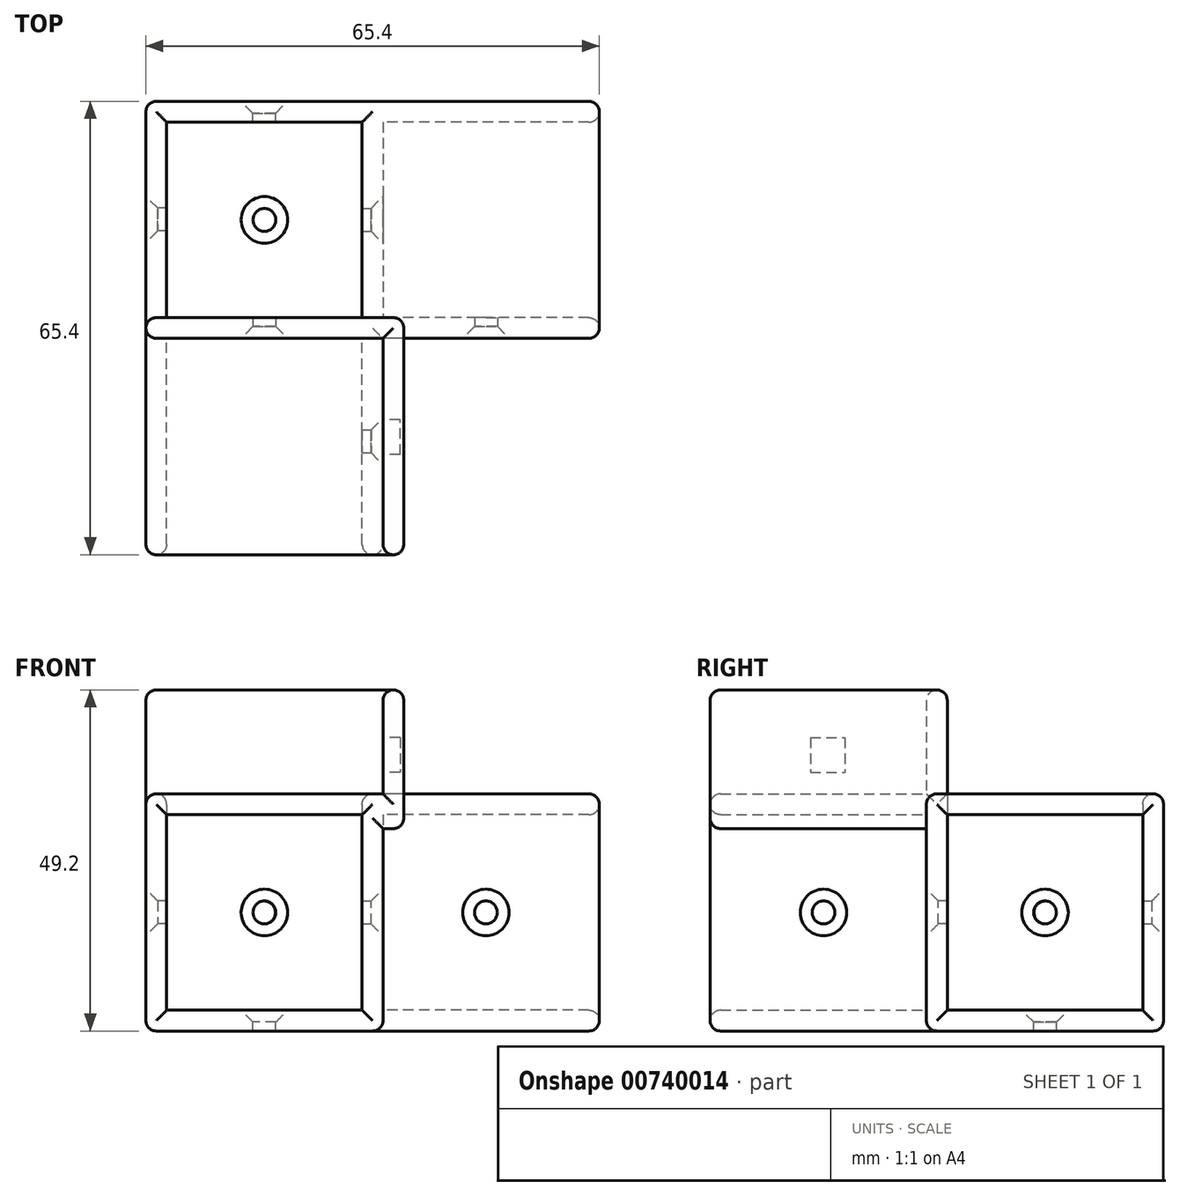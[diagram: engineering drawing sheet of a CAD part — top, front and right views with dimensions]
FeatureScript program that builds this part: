
annotation { "Feature Type Name" : "Feature", "Feature Type Description" : "" }
export const myFeature = defineFeature(function(context is Context, id is Id, definition is map)
    precondition{}
    {
        {
            var Q0;
            Q0=qCreatedBy(makeId("Top.planeOp"),FACE);
            var sketch = newSketch(context, id + "F0", { "sketchPlane" : qUnion([Q0])});
            skLineSegment(sketch, "E0.bottom", {"start": v(0, 0) * mm, "end": v(-28.2, 0) * mm});
            skLineSegment(sketch, "E0.top", {"start": v(0, 28.2) * mm, "end": v(-28.2, 28.2) * mm});
            skLineSegment(sketch, "E0.left", {"start": v(0, 0) * mm, "end": v(0, 28.2) * mm});
            skLineSegment(sketch, "E0.right", {"start": v(-28.2, 0) * mm, "end": v(-28.2, 28.2) * mm});
            skLineSegment(sketch, "E1.0", {"start": v(3, 31.2) * mm, "end": v(-31.2, 31.2) * mm});
            skLineSegment(sketch, "E1.1", {"start": v(3, -3) * mm, "end": v(3, 31.2) * mm});
            skLineSegment(sketch, "E1.2", {"start": v(3, -3) * mm, "end": v(-31.2, -3) * mm});
            skLineSegment(sketch, "E1.3", {"start": v(-31.2, -3) * mm, "end": v(-31.2, 31.2) * mm});
            skPoint(sketch, "E2", {"position": v(-14.1, 14.1) * mm});
            skSolve(sketch);
        }
        {
            var Q0;
            Q0=makeQuery(id+"F0.imprint","IMPRINT",FACE,{"disambiguationData":[TD([[makeQuery(id+"F0.imprint","IMPRINT",EDGE,{"derivedFrom":sQuery(id+"F0.wireOp",EDGE,"E0.bottom")}),1.0]])]});
            var Q1;
            Q1=makeQuery(id+"F0.imprint","IMPRINT",FACE,{"disambiguationData":[TD([[makeQuery(id+"F0.imprint","IMPRINT",EDGE,{"derivedFrom":sQuery(id+"F0.wireOp",EDGE,"E0.bottom")}),-1.0]])]});
            extrude(context, id + "F1", {"entities" : qUnion([Q0, Q1]), "oppositeDirection" : true, "depth" : 3 * mm, "offsetDistance" : 25 * mm});
        }
        {
            var Q0;
            Q0=makeQuery(id+"F0.imprint","IMPRINT",FACE,{"disambiguationData":[TD([[makeQuery(id+"F0.imprint","IMPRINT",EDGE,{"derivedFrom":sQuery(id+"F0.wireOp",EDGE,"E0.bottom")}),1.0]])]});
            extrude(context, id + "F2", {"entities" : qUnion([Q0]), "operationType" : NewBodyOperationType.ADD, "depth" : 31.2 * mm, "offsetDistance" : 25 * mm});
        }
        {
            var Q0;
            {var subQ0=sQuery(id+"F0.wireOp",EDGE,"E1.2");Q0=makeQuery(id+"F2.boolean.opBoolean","MERGE",FACE,{"derivedFrom":[makeQuery(id+"F1.opExtrude","SWEPT_FACE",FACE,{"disambiguationData":[OSD([subQ0])]}),makeQuery(id+"F2.opExtrude","SWEPT_FACE",FACE,{"disambiguationData":[OSD([subQ0])]})]});}
            var sketch = newSketch(context, id + "F3", { "sketchPlane" : qUnion([Q0])});
            skLineSegment(sketch, "E3.bottom", {"start": v(-31.2, 31.2) * mm, "end": v(3, 31.2) * mm});
            skLineSegment(sketch, "E3.top", {"start": v(-31.2, -3) * mm, "end": v(3, -3) * mm});
            skLineSegment(sketch, "E3.left", {"start": v(-31.2, 31.2) * mm, "end": v(-31.2, -3) * mm});
            skLineSegment(sketch, "E3.right", {"start": v(3, 31.2) * mm, "end": v(3, -3) * mm});
            skLineSegment(sketch, "E4.0", {"start": v(-28.2, 28.2) * mm, "end": v(0, 28.2) * mm});
            skLineSegment(sketch, "E4.1", {"start": v(-28.2, 28.2) * mm, "end": v(-28.2, 0) * mm});
            skLineSegment(sketch, "E4.2", {"start": v(-28.2, 0) * mm, "end": v(0, 0) * mm});
            skLineSegment(sketch, "E4.3", {"start": v(0, 28.2) * mm, "end": v(0, 0) * mm});
            skPoint(sketch, "E5", {"position": v(-14.1, 14.1) * mm});
            skSolve(sketch);
        }
        {
            var Q0;
            Q0=makeQuery(id+"F3.imprint","IMPRINT",FACE,{"disambiguationData":[TD([[makeQuery(id+"F3.imprint","IMPRINT",EDGE,{"derivedFrom":sQuery(id+"F3.wireOp",EDGE,"E3.bottom")}),1.0]])]});
            extrude(context, id + "F4", {"entities" : qUnion([Q0]), "operationType" : NewBodyOperationType.ADD, "depth" : 31.2 * mm, "offsetDistance" : 25 * mm});
        }
        {
            var Q0;
            {var subQ0=sQuery(id+"F0.wireOp",EDGE,"E1.1");Q0=makeQuery(id+"F4.boolean.opBoolean","MERGE",FACE,{"derivedFrom":[makeQuery(id+"F2.boolean.opBoolean","MERGE",FACE,{"derivedFrom":[makeQuery(id+"F1.opExtrude","SWEPT_FACE",FACE,{"disambiguationData":[OSD([subQ0])]}),makeQuery(id+"F2.opExtrude","SWEPT_FACE",FACE,{"disambiguationData":[OSD([subQ0])]})]}),makeQuery(id+"F4.opExtrude","SWEPT_FACE",FACE,{"disambiguationData":[OSD([sQuery(id+"F3.wireOp",EDGE,"E3.right")])]})]});}
            var sketch = newSketch(context, id + "F5", { "sketchPlane" : qUnion([Q0])});
            skLineSegment(sketch, "E6.bottom", {"start": v(31.2, 31.2) * mm, "end": v(-3, 31.2) * mm});
            skLineSegment(sketch, "E6.top", {"start": v(31.2, -3) * mm, "end": v(-3, -3) * mm});
            skLineSegment(sketch, "E6.left", {"start": v(31.2, 31.2) * mm, "end": v(31.2, -3) * mm});
            skLineSegment(sketch, "E6.right", {"start": v(-3, 31.2) * mm, "end": v(-3, -3) * mm});
            skLineSegment(sketch, "E7.0", {"start": v(28.2, 28.2) * mm, "end": v(0, 28.2) * mm});
            skLineSegment(sketch, "E7.1", {"start": v(28.2, 28.2) * mm, "end": v(28.2, 0) * mm});
            skLineSegment(sketch, "E7.2", {"start": v(28.2, 0) * mm, "end": v(0, 0) * mm});
            skLineSegment(sketch, "E7.3", {"start": v(0, 28.2) * mm, "end": v(0, 0) * mm});
            skPoint(sketch, "E8", {"position": v(14.1, 14.1) * mm});
            skSolve(sketch);
        }
        {
            var Q0;
            Q0=qSketchRegion(id+"F5",true);
            extrude(context, id + "F6", {"entities" : qUnion([Q0]), "operationType" : NewBodyOperationType.ADD, "depth" : 31.2 * mm, "offsetDistance" : 25 * mm});
        }
        {
            var Q0;
            Q0=sQuery(id+"F0.wireOp",VERTEX,"E2");
            var Q1;
            Q1=sQuery(id+"F5.wireOp",VERTEX,"E8");
            var Q2;
            Q2=sQuery(id+"F3.wireOp",VERTEX,"E5");
            var Q3;
            Q3=makeQuery(id+"F1.opExtrude","SWEPT_BODY",BODY,{"disambiguationData":[OSD([sQuery(id+"F0.wireOp",EDGE,"E1.0"),sQuery(id+"F0.wireOp",EDGE,"E1.1"),sQuery(id+"F0.wireOp",EDGE,"E1.2"),sQuery(id+"F0.wireOp",EDGE,"E1.3")])]});
            hole(context, id + "F7", {"style" : HoleStyle.C_SINK, "endStyle" : HoleEndStyle.BLIND, "standardTappedOrClearance" : lookupTablePath({ "standard" : "ISO", "fit" : "Normal", "size" : "M3", "type" : "Clearance" }), "standardBlindInLast" : lookupTablePath({ "fit" : "Standard", "standard" : "ISO", "size" : "M3", "type" : "Clearance" }), "holeDiameter" : 3.3 * mm, "cSinkDiameter" : 6.72 * mm, "cSinkAngle" : 90 * degree, "majorDiameter" : 5 * mm, "holeDepth" : 13.5 * mm, "isTappedThrough" : true, "tappedDepth" : 12 * mm, "tapClearance" : 3, "startFromSketch" : true, "locations" : qUnion([Q0, Q1, Q2]), "scope" : qUnion([Q3])});
        }
        {
            var Q0;
            {var subQ0=sQuery(id+"F3.wireOp",EDGE,"E3.bottom");var subQ3=sQuery(id+"F0.wireOp",EDGE,"E1.1");var subQ5=sQuery(id+"F3.wireOp",EDGE,"E3.right");Q0=makeQuery(id+"F6.boolean.opBoolean","SPLIT",FACE,{"disambiguationData":[TD([makeQuery(id+"F4.opExtrude","SWEPT_FACE",FACE,{"disambiguationData":[OSD([subQ0])]})])],"derivedFrom":makeQuery(id+"F4.boolean.opBoolean","MERGE",FACE,{"derivedFrom":[makeQuery(id+"F2.boolean.opBoolean","MERGE",FACE,{"derivedFrom":[makeQuery(id+"F1.opExtrude","SWEPT_FACE",FACE,{"disambiguationData":[OSD([subQ3])]}),makeQuery(id+"F2.opExtrude","SWEPT_FACE",FACE,{"disambiguationData":[OSD([subQ3])]})]}),makeQuery(id+"F4.opExtrude","SWEPT_FACE",FACE,{"disambiguationData":[OSD([subQ5])]})]})});}
            var sketch = newSketch(context, id + "F8", { "sketchPlane" : qUnion([Q0])});
            skPoint(sketch, "E9", {"position": v(-17.85, 14.1) * mm});
            skSolve(sketch);
        }
        {
            var Q0;
            Q0=makeQuery(id+"F6.opExtrude","SWEPT_FACE",FACE,{"disambiguationData":[OSD([sQuery(id+"F5.wireOp",EDGE,"E6.right")])]});
            var sketch = newSketch(context, id + "F9", { "sketchPlane" : qUnion([Q0])});
            skPoint(sketch, "E10", {"position": v(17.85, 14.1) * mm});
            skSolve(sketch);
        }
        {
            var Q0;
            Q0=sQuery(id+"F9.wireOp",VERTEX,"E10");
            var Q1;
            Q1=sQuery(id+"F8.wireOp",VERTEX,"E9");
            var Q2;
            Q2=makeQuery(id+"F1.opExtrude","SWEPT_BODY",BODY,{"disambiguationData":[OSD([sQuery(id+"F0.wireOp",EDGE,"E1.0"),sQuery(id+"F0.wireOp",EDGE,"E1.1"),sQuery(id+"F0.wireOp",EDGE,"E1.2"),sQuery(id+"F0.wireOp",EDGE,"E1.3")])]});
            hole(context, id + "F10", {"style" : HoleStyle.C_SINK, "endStyle" : HoleEndStyle.BLIND, "standardTappedOrClearance" : lookupTablePath({ "standard" : "ISO", "fit" : "Normal", "size" : "M3", "type" : "Clearance" }), "standardBlindInLast" : lookupTablePath({ "fit" : "Standard", "standard" : "ISO", "size" : "M3", "type" : "Clearance" }), "holeDiameter" : 3.3 * mm, "cSinkDiameter" : 6.72 * mm, "cSinkAngle" : 90 * degree, "majorDiameter" : 5 * mm, "holeDepth" : 13.5 * mm, "isTappedThrough" : true, "tappedDepth" : 12 * mm, "tapClearance" : 3, "startFromSketch" : true, "locations" : qUnion([Q0, Q1]), "scope" : qUnion([Q2])});
        }
        {
            var Q0;
            Q0=makeQuery(id+"F6.boolean.opBoolean","MERGE",FACE,{"derivedFrom":[makeQuery(id+"F4.boolean.opBoolean","MERGE",FACE,{"derivedFrom":[makeQuery(id+"F2.opExtrude","CAP_FACE",FACE,{"disambiguationData":[OSD([sQuery(id+"F0.wireOp",EDGE,"E0.bottom"),sQuery(id+"F0.wireOp",EDGE,"E0.top"),sQuery(id+"F0.wireOp",EDGE,"E0.left"),sQuery(id+"F0.wireOp",EDGE,"E0.right"),sQuery(id+"F0.wireOp",EDGE,"E1.0"),sQuery(id+"F0.wireOp",EDGE,"E1.1"),sQuery(id+"F0.wireOp",EDGE,"E1.2"),sQuery(id+"F0.wireOp",EDGE,"E1.3")])],"isStart":false}),makeQuery(id+"F4.opExtrude","SWEPT_FACE",FACE,{"disambiguationData":[OSD([sQuery(id+"F3.wireOp",EDGE,"E3.bottom")])]})]}),makeQuery(id+"F6.opExtrude","SWEPT_FACE",FACE,{"disambiguationData":[OSD([sQuery(id+"F5.wireOp",EDGE,"E6.bottom")])]})]});
            var sketch = newSketch(context, id + "F11", { "sketchPlane" : qUnion([Q0])});
            skLineSegment(sketch, "E11.bottom", {"start": v(6, 0) * mm, "end": v(-31.2, 0) * mm});
            skLineSegment(sketch, "E11.top", {"start": v(6, -3) * mm, "end": v(-31.2, -3) * mm});
            skLineSegment(sketch, "E11.right", {"start": v(-31.2, 0) * mm, "end": v(-31.2, -3) * mm});
            skLineSegment(sketch, "E12", {"start": v(6, -3) * mm, "end": v(6, 0) * mm});
            skSolve(sketch);
        }
        {
            var Q0;
            {var subQ5=sQuery(id+"F11.wireOp",EDGE,"E11.right");Q0=makeQuery(id+"F11.imprint","IMPRINT",FACE,{"disambiguationData":[TD([[makeQuery(id+"F11.imprint","IMPRINT",EDGE,{"derivedFrom":subQ5}),-1.0]])]});}
            extrude(context, id + "F12", {"entities" : qUnion([Q0]), "operationType" : NewBodyOperationType.ADD, "depth" : 15 * mm, "offsetDistance" : 25 * mm});
        }
        {
            var Q0;
            {var subQ0=sQuery(id+"F0.wireOp",EDGE,"E1.3");Q0=makeQuery(id+"F4.boolean.opBoolean","MERGE",FACE,{"derivedFrom":[makeQuery(id+"F2.boolean.opBoolean","MERGE",FACE,{"derivedFrom":[makeQuery(id+"F1.opExtrude","SWEPT_FACE",FACE,{"disambiguationData":[OSD([subQ0])]}),makeQuery(id+"F2.opExtrude","SWEPT_FACE",FACE,{"disambiguationData":[OSD([subQ0])]})]}),makeQuery(id+"F4.opExtrude","SWEPT_FACE",FACE,{"disambiguationData":[OSD([sQuery(id+"F3.wireOp",EDGE,"E3.left")])]})]});}
            var sketch = newSketch(context, id + "F13", { "sketchPlane" : qUnion([Q0])});
            skPoint(sketch, "E13", {"position": v(-14.15, 14.1) * mm});
            skSolve(sketch);
        }
        {
            var Q0;
            {var subQ0=sQuery(id+"F0.wireOp",EDGE,"E1.0");Q0=makeQuery(id+"F6.boolean.opBoolean","MERGE",FACE,{"derivedFrom":[makeQuery(id+"F2.boolean.opBoolean","MERGE",FACE,{"derivedFrom":[makeQuery(id+"F1.opExtrude","SWEPT_FACE",FACE,{"disambiguationData":[OSD([subQ0])]}),makeQuery(id+"F2.opExtrude","SWEPT_FACE",FACE,{"disambiguationData":[OSD([subQ0])]})]}),makeQuery(id+"F6.opExtrude","SWEPT_FACE",FACE,{"disambiguationData":[OSD([sQuery(id+"F5.wireOp",EDGE,"E6.left")])]})]});}
            var sketch = newSketch(context, id + "F14", { "sketchPlane" : qUnion([Q0])});
            skPoint(sketch, "E14", {"position": v(14.15, 14.1) * mm});
            skPoint(sketch, "E14.positionSnap0", {"position": v(31.2, 14.1) * mm});
            skSolve(sketch);
        }
        {
            var Q0;
            Q0=sQuery(id+"F13.wireOp",VERTEX,"E13");
            var Q1;
            Q1=sQuery(id+"F14.wireOp",VERTEX,"E14");
            var Q2;
            Q2=makeQuery(id+"F1.opExtrude","SWEPT_BODY",BODY,{"disambiguationData":[OSD([sQuery(id+"F0.wireOp",EDGE,"E1.0"),sQuery(id+"F0.wireOp",EDGE,"E1.1"),sQuery(id+"F0.wireOp",EDGE,"E1.2"),sQuery(id+"F0.wireOp",EDGE,"E1.3")])]});
            hole(context, id + "F15", {"style" : HoleStyle.C_SINK, "endStyle" : HoleEndStyle.BLIND, "standardTappedOrClearance" : lookupTablePath({ "standard" : "ISO", "fit" : "Normal", "size" : "M3", "type" : "Clearance" }), "standardBlindInLast" : lookupTablePath({ "fit" : "Standard", "standard" : "ISO", "size" : "M3", "type" : "Clearance" }), "holeDiameter" : 3.3 * mm, "cSinkDiameter" : 6.72 * mm, "cSinkAngle" : 90 * degree, "majorDiameter" : 5 * mm, "holeDepth" : 13.5 * mm, "isTappedThrough" : true, "tappedDepth" : 12 * mm, "tapClearance" : 3, "startFromSketch" : true, "locations" : qUnion([Q0, Q1]), "scope" : qUnion([Q2])});
        }
        {
            var Q0;
            {var subQ0=sQuery(id+"F3.wireOp",EDGE,"E3.bottom");var subQ3=sQuery(id+"F0.wireOp",EDGE,"E1.1");var subQ5=sQuery(id+"F3.wireOp",EDGE,"E3.right");Q0=makeQuery(id+"F6.boolean.opBoolean","SPLIT",FACE,{"disambiguationData":[TD([makeQuery(id+"F4.opExtrude","SWEPT_FACE",FACE,{"disambiguationData":[OSD([subQ0])]})])],"derivedFrom":makeQuery(id+"F4.boolean.opBoolean","MERGE",FACE,{"derivedFrom":[makeQuery(id+"F2.boolean.opBoolean","MERGE",FACE,{"derivedFrom":[makeQuery(id+"F1.opExtrude","SWEPT_FACE",FACE,{"disambiguationData":[OSD([subQ3])]}),makeQuery(id+"F2.opExtrude","SWEPT_FACE",FACE,{"disambiguationData":[OSD([subQ3])]})]}),makeQuery(id+"F4.opExtrude","SWEPT_FACE",FACE,{"disambiguationData":[OSD([subQ5])]})]})});}
            var sketch = newSketch(context, id + "F16", { "sketchPlane" : qUnion([Q0])});
            skLineSegment(sketch, "E15.bottom", {"start": v(-34.2, 26.2) * mm, "end": v(-3, 26.2) * mm});
            skLineSegment(sketch, "E15.top", {"start": v(-34.2, 46.2) * mm, "end": v(-3, 46.2) * mm});
            skLineSegment(sketch, "E15.left", {"start": v(-34.2, 26.2) * mm, "end": v(-34.2, 46.2) * mm});
            skLineSegment(sketch, "E15.right", {"start": v(-3, 26.2) * mm, "end": v(-3, 46.2) * mm});
            skSolve(sketch);
        }
        {
            var Q0;
            {var subQ0=sQuery(id+"F16.wireOp",EDGE,"E15.bottom");Q0=makeQuery(id+"F16.imprint","IMPRINT",FACE,{"disambiguationData":[TD([[makeQuery(id+"F16.imprint","IMPRINT",EDGE,{"derivedFrom":subQ0}),1.0]])]});}
            var Q1;
            {var subQ0=sQuery(id+"F16.wireOp",EDGE,"E15.top");Q1=makeQuery(id+"F16.imprint","IMPRINT",FACE,{"disambiguationData":[TD([[makeQuery(id+"F16.imprint","IMPRINT",EDGE,{"derivedFrom":subQ0}),-1.0]])]});}
            extrude(context, id + "F17", {"entities" : qUnion([Q0, Q1]), "operationType" : NewBodyOperationType.ADD, "depth" : 3 * mm, "offsetDistance" : 25 * mm});
        }
        {
            var Q0;
            Q0=makeQuery(id+"F12.opExtrude","SWEPT_EDGE",EDGE,{"disambiguationData":[OSD([sQuery(id+"F0.wireOp",EDGE,"E1.3"),sQuery(id+"F3.wireOp",EDGE,"E3.bottom"),sQuery(id+"F3.wireOp",EDGE,"E3.left"),sQuery(id+"F11.wireOp",EDGE,"E11.bottom"),sQuery(id+"F11.wireOp",EDGE,"E11.right")])]});
            var Q1;
            Q1=makeQuery(id+"F12.opExtrude","SWEPT_EDGE",EDGE,{"disambiguationData":[OSD([sQuery(id+"F0.wireOp",EDGE,"E1.3"),sQuery(id+"F3.wireOp",EDGE,"E3.bottom"),sQuery(id+"F3.wireOp",EDGE,"E3.left"),sQuery(id+"F11.wireOp",EDGE,"E11.top"),sQuery(id+"F11.wireOp",EDGE,"E11.right")])]});
            var Q2;
            Q2=makeQuery(id+"F12.opExtrude","CAP_EDGE",EDGE,{"disambiguationData":[OSD([sQuery(id+"F11.wireOp",EDGE,"E11.right")])],"isStart":false});
            var Q3;
            Q3=makeQuery(id+"F17.opExtrude","SWEPT_EDGE",EDGE,{"disambiguationData":[OSD([sQuery(id+"F16.wireOp",EDGE,"E15.top"),sQuery(id+"F16.wireOp",EDGE,"E15.left")])]});
            var Q4;
            Q4=makeQuery(id+"F17.opExtrude","CAP_EDGE",EDGE,{"disambiguationData":[OSD([sQuery(id+"F16.wireOp",EDGE,"E15.left")])],"isStart":true});
            var Q5;
            Q5=makeQuery(id+"F17.opExtrude","CAP_EDGE",EDGE,{"disambiguationData":[OSD([sQuery(id+"F16.wireOp",EDGE,"E15.top")])],"isStart":true});
            var Q6;
            Q6=makeQuery(id+"F12.opExtrude","CAP_EDGE",EDGE,{"disambiguationData":[OSD([sQuery(id+"F11.wireOp",EDGE,"E11.top")])],"isStart":false});
            var Q7;
            Q7=makeQuery(id+"F12.opExtrude","CAP_EDGE",EDGE,{"disambiguationData":[OSD([sQuery(id+"F11.wireOp",EDGE,"E11.bottom")])],"isStart":false});
            var Q8;
            Q8=makeQuery(id+"F17.opExtrude","CAP_EDGE",EDGE,{"disambiguationData":[OSD([sQuery(id+"F16.wireOp",EDGE,"E15.left")])],"isStart":false});
            var Q9;
            Q9=makeQuery(id+"F17.boolean.opBoolean","MERGE",EDGE,{"derivedFrom":[makeQuery(id+"F12.opExtrude","CAP_EDGE",EDGE,{"disambiguationData":[OSD([sQuery(id+"F11.wireOp",EDGE,"E12")])],"isStart":false}),makeQuery(id+"F17.opExtrude","CAP_EDGE",EDGE,{"disambiguationData":[OSD([sQuery(id+"F16.wireOp",EDGE,"E15.top")])],"isStart":false})]});
            var Q10;
            Q10=makeQuery(id+"F4.opExtrude","CAP_EDGE",EDGE,{"disambiguationData":[OSD([sQuery(id+"F3.wireOp",EDGE,"E3.bottom")])],"isStart":false});
            var Q11;
            Q11=makeQuery(id+"F4.opExtrude","CAP_EDGE",EDGE,{"disambiguationData":[OSD([sQuery(id+"F3.wireOp",EDGE,"E3.left")])],"isStart":false});
            var Q12;
            Q12=makeQuery(id+"F4.opExtrude","CAP_EDGE",EDGE,{"disambiguationData":[OSD([sQuery(id+"F3.wireOp",EDGE,"E4.1")])],"isStart":false});
            var Q13;
            Q13=makeQuery(id+"F4.opExtrude","CAP_EDGE",EDGE,{"disambiguationData":[OSD([sQuery(id+"F3.wireOp",EDGE,"E3.top")])],"isStart":false});
            var Q14;
            Q14=makeQuery(id+"F4.opExtrude","CAP_EDGE",EDGE,{"disambiguationData":[OSD([sQuery(id+"F3.wireOp",EDGE,"E4.2")])],"isStart":true});
            var Q15;
            Q15=makeQuery(id+"F4.opExtrude","CAP_EDGE",EDGE,{"disambiguationData":[OSD([sQuery(id+"F3.wireOp",EDGE,"E3.right")])],"isStart":false});
            var Q16;
            Q16=makeQuery(id+"F4.opExtrude","CAP_EDGE",EDGE,{"disambiguationData":[OSD([sQuery(id+"F3.wireOp",EDGE,"E4.3")])],"isStart":false});
            var Q17;
            Q17=makeQuery(id+"F17.opExtrude","CAP_EDGE",EDGE,{"disambiguationData":[OSD([sQuery(id+"F16.wireOp",EDGE,"E15.bottom")])],"isStart":false});
            var Q18;
            Q18=makeQuery(id+"F17.opExtrude","CAP_EDGE",EDGE,{"disambiguationData":[OSD([sQuery(id+"F16.wireOp",EDGE,"E15.bottom")])],"isStart":true});
            var Q19;
            Q19=makeQuery(id+"F17.opExtrude","CAP_EDGE",EDGE,{"disambiguationData":[OSD([sQuery(id+"F16.wireOp",EDGE,"E15.right")])],"isStart":false});
            var Q20;
            Q20=makeQuery(id+"F6.opExtrude","CAP_EDGE",EDGE,{"disambiguationData":[OSD([sQuery(id+"F5.wireOp",EDGE,"E6.right")])],"isStart":true});
            var Q21;
            Q21=makeQuery(id+"F4.boolean.opBoolean","MERGE",EDGE,{"derivedFrom":[makeQuery(id+"F1.opExtrude","CAP_EDGE",EDGE,{"disambiguationData":[OSD([sQuery(id+"F0.wireOp",EDGE,"E1.1")])],"isStart":false}),makeQuery(id+"F4.opExtrude","SWEPT_EDGE",EDGE,{"disambiguationData":[OSD([sQuery(id+"F3.wireOp",EDGE,"E3.top"),sQuery(id+"F3.wireOp",EDGE,"E3.right")])]})]});
            var Q22;
            Q22=makeQuery(id+"F4.boolean.opBoolean","MERGE",EDGE,{"derivedFrom":[makeQuery(id+"F1.opExtrude","CAP_EDGE",EDGE,{"disambiguationData":[OSD([sQuery(id+"F0.wireOp",EDGE,"E1.3")])],"isStart":false}),makeQuery(id+"F4.opExtrude","SWEPT_EDGE",EDGE,{"disambiguationData":[OSD([sQuery(id+"F3.wireOp",EDGE,"E3.top"),sQuery(id+"F3.wireOp",EDGE,"E3.left")])]})]});
            var Q23;
            Q23=makeQuery(id+"F6.opExtrude","SWEPT_EDGE",EDGE,{"disambiguationData":[OSD([sQuery(id+"F0.wireOp",EDGE,"E1.1"),sQuery(id+"F3.wireOp",EDGE,"E3.bottom"),sQuery(id+"F3.wireOp",EDGE,"E3.right"),sQuery(id+"F5.wireOp",EDGE,"E6.bottom"),sQuery(id+"F5.wireOp",EDGE,"E6.right")])]});
            var Q24;
            Q24=makeQuery(id+"F6.opExtrude","CAP_EDGE",EDGE,{"disambiguationData":[OSD([sQuery(id+"F5.wireOp",EDGE,"E6.right")])],"isStart":false});
            var Q25;
            Q25=makeQuery(id+"F6.opExtrude","CAP_EDGE",EDGE,{"disambiguationData":[OSD([sQuery(id+"F5.wireOp",EDGE,"E7.3")])],"isStart":false});
            var Q26;
            Q26=makeQuery(id+"F6.opExtrude","CAP_EDGE",EDGE,{"disambiguationData":[OSD([sQuery(id+"F5.wireOp",EDGE,"E6.top")])],"isStart":false});
            var Q27;
            Q27=makeQuery(id+"F6.opExtrude","CAP_EDGE",EDGE,{"disambiguationData":[OSD([sQuery(id+"F5.wireOp",EDGE,"E7.2")])],"isStart":false});
            var Q28;
            Q28=makeQuery(id+"F6.opExtrude","CAP_EDGE",EDGE,{"disambiguationData":[OSD([sQuery(id+"F5.wireOp",EDGE,"E6.left")])],"isStart":false});
            var Q29;
            Q29=makeQuery(id+"F6.opExtrude","CAP_EDGE",EDGE,{"disambiguationData":[OSD([sQuery(id+"F5.wireOp",EDGE,"E7.1")])],"isStart":false});
            var Q30;
            Q30=makeQuery(id+"F6.opExtrude","CAP_EDGE",EDGE,{"disambiguationData":[OSD([sQuery(id+"F5.wireOp",EDGE,"E7.0")])],"isStart":false});
            var Q31;
            Q31=makeQuery(id+"F2.opExtrude","CAP_EDGE",EDGE,{"disambiguationData":[OSD([sQuery(id+"F0.wireOp",EDGE,"E0.left")])],"isStart":false});
            var Q32;
            Q32=makeQuery(id+"F2.opExtrude","CAP_EDGE",EDGE,{"disambiguationData":[OSD([sQuery(id+"F0.wireOp",EDGE,"E0.top")])],"isStart":false});
            var Q33;
            Q33=makeQuery(id+"F6.boolean.opBoolean","MERGE",EDGE,{"derivedFrom":[makeQuery(id+"F2.opExtrude","CAP_EDGE",EDGE,{"disambiguationData":[OSD([sQuery(id+"F0.wireOp",EDGE,"E1.0")])],"isStart":false}),makeQuery(id+"F6.opExtrude","SWEPT_EDGE",EDGE,{"disambiguationData":[OSD([sQuery(id+"F5.wireOp",EDGE,"E6.bottom"),sQuery(id+"F5.wireOp",EDGE,"E6.left")])]})]});
            var Q34;
            Q34=makeQuery(id+"F2.opExtrude","CAP_EDGE",EDGE,{"disambiguationData":[OSD([sQuery(id+"F0.wireOp",EDGE,"E0.right")])],"isStart":false});
            var Q35;
            {var subQ0=sQuery(id+"F0.wireOp",EDGE,"E1.3");var subQ1=sQuery(id+"F0.wireOp",EDGE,"E1.0");Q35=makeQuery(id+"F2.boolean.opBoolean","MERGE",EDGE,{"derivedFrom":[makeQuery(id+"F1.opExtrude","SWEPT_EDGE",EDGE,{"disambiguationData":[OSD([subQ1,subQ0])]}),makeQuery(id+"F2.opExtrude","SWEPT_EDGE",EDGE,{"disambiguationData":[OSD([subQ1,subQ0])]})]});}
            var Q36;
            Q36=makeQuery(id+"F6.boolean.opBoolean","MERGE",EDGE,{"derivedFrom":[makeQuery(id+"F1.opExtrude","CAP_EDGE",EDGE,{"disambiguationData":[OSD([sQuery(id+"F0.wireOp",EDGE,"E1.0")])],"isStart":false}),makeQuery(id+"F6.opExtrude","SWEPT_EDGE",EDGE,{"disambiguationData":[OSD([sQuery(id+"F5.wireOp",EDGE,"E6.top"),sQuery(id+"F5.wireOp",EDGE,"E6.left")])]})]});
            var Q37;
            Q37=makeQuery(id+"F6.opExtrude","SWEPT_EDGE",EDGE,{"disambiguationData":[OSD([sQuery(id+"F0.wireOp",EDGE,"E1.1"),sQuery(id+"F3.wireOp",EDGE,"E3.top"),sQuery(id+"F3.wireOp",EDGE,"E3.right"),sQuery(id+"F5.wireOp",EDGE,"E6.top"),sQuery(id+"F5.wireOp",EDGE,"E6.right")])]});
            var Q38;
            {var subQ0=sQuery(id+"F0.wireOp",EDGE,"E0.left");var subQ1=sQuery(id+"F11.wireOp",EDGE,"E11.bottom");Q38=makeQuery(id+"F12.boolean.opBoolean","SPLIT",EDGE,{"disambiguationData":[TD([makeQuery(id+"F2.opExtrude","SWEPT_FACE",FACE,{"disambiguationData":[OSD([subQ0])]})])],"derivedFrom":makeQuery(id+"F12.opExtrude","CAP_EDGE",EDGE,{"disambiguationData":[OSD([subQ1])],"isStart":true})});}
            var Q39;
            Q39=makeQuery(id+"F12.opExtrude","SWEPT_EDGE",EDGE,{"disambiguationData":[OSD([sQuery(id+"F11.wireOp",EDGE,"E11.bottom"),sQuery(id+"F11.wireOp",EDGE,"E12")])]});
            var Q40;
            {var subQ0=sQuery(id+"F0.wireOp",EDGE,"E1.3");var subQ1=sQuery(id+"F3.wireOp",EDGE,"E3.bottom");var subQ2=sQuery(id+"F3.wireOp",EDGE,"E3.left");Q40=makeQuery(id+"F12.boolean.opBoolean","SPLIT",EDGE,{"disambiguationData":[TD([makeQuery(id+"F6.opExtrude","SWEPT_FACE",FACE,{"disambiguationData":[OSD([sQuery(id+"F5.wireOp",EDGE,"E6.right")])]})])],"derivedFrom":makeQuery(id+"F4.boolean.opBoolean","MERGE",EDGE,{"derivedFrom":[makeQuery(id+"F2.opExtrude","CAP_EDGE",EDGE,{"disambiguationData":[OSD([subQ0])],"isStart":false}),makeQuery(id+"F4.opExtrude","SWEPT_EDGE",EDGE,{"disambiguationData":[OSD([subQ1,subQ2])]})]})});}
            var Q41;
            {var subQ0=sQuery(id+"F3.wireOp",EDGE,"E3.bottom");var subQ1=sQuery(id+"F3.wireOp",EDGE,"E3.left");var subQ2=sQuery(id+"F0.wireOp",EDGE,"E1.3");var subQ3=sQuery(id+"F0.wireOp",EDGE,"E1.0");Q41=makeQuery(id+"F12.boolean.opBoolean","SPLIT",EDGE,{"disambiguationData":[TD([makeQuery(id+"F1.opExtrude","SWEPT_FACE",FACE,{"disambiguationData":[OSD([subQ3])]})])],"derivedFrom":makeQuery(id+"F4.boolean.opBoolean","MERGE",EDGE,{"derivedFrom":[makeQuery(id+"F2.opExtrude","CAP_EDGE",EDGE,{"disambiguationData":[OSD([subQ2])],"isStart":false}),makeQuery(id+"F4.opExtrude","SWEPT_EDGE",EDGE,{"disambiguationData":[OSD([subQ0,subQ1])]})]})});}
            var Q42;
            Q42=makeQuery(id+"F17.opExtrude","SWEPT_EDGE",EDGE,{"disambiguationData":[OSD([sQuery(id+"F3.wireOp",EDGE,"E3.right"),sQuery(id+"F16.wireOp",EDGE,"E15.bottom"),sQuery(id+"F16.wireOp",EDGE,"E15.left")])]});
            var Q43;
            Q43=makeQuery(id+"F4.opExtrude","CAP_EDGE",EDGE,{"disambiguationData":[OSD([sQuery(id+"F3.wireOp",EDGE,"E4.0")])],"isStart":false});
            var Q44;
            Q44=makeQuery(id+"F4.opExtrude","CAP_EDGE",EDGE,{"disambiguationData":[OSD([sQuery(id+"F3.wireOp",EDGE,"E4.2")])],"isStart":false});
            var Q45;
            Q45=makeQuery(id+"F6.opExtrude","CAP_EDGE",EDGE,{"disambiguationData":[OSD([sQuery(id+"F5.wireOp",EDGE,"E6.bottom")])],"isStart":false});
            fillet(context, id + "F18", {"entities" : qUnion([Q0, Q1, Q2, Q3, Q4, Q5, Q6, Q7, Q8, Q9, Q10, Q11, Q12, Q13, Q14, Q15, Q16, Q17, Q18, Q19, Q20, Q21, Q22, Q23, Q24, Q25, Q26, Q27, Q28, Q29, Q30, Q31, Q32, Q33, Q34, Q35, Q36, Q37, Q38, Q39, Q40, Q41, Q42, Q43, Q44, Q45]), "radius" : 1.5 * mm, "tangentPropagation" : true, "allowEdgeOverflow" : false});
        }
        {
            var Q0;
            Q0=makeQuery(id+"F17.opExtrude","CAP_FACE",FACE,{"disambiguationData":[OSD([sQuery(id+"F16.wireOp",EDGE,"E15.bottom"),sQuery(id+"F16.wireOp",EDGE,"E15.top"),sQuery(id+"F16.wireOp",EDGE,"E15.left"),sQuery(id+"F16.wireOp",EDGE,"E15.right")])],"isStart":true});
            var sketch = newSketch(context, id + "F19", { "sketchPlane" : qUnion([Q0])});
            skLineSegment(sketch, "E16.bottom", {"start": v(19.75, 39.33) * mm, "end": v(14.75, 39.33) * mm});
            skLineSegment(sketch, "E16.top", {"start": v(19.75, 34.33) * mm, "end": v(14.75, 34.33) * mm});
            skLineSegment(sketch, "E16.left", {"start": v(19.75, 39.33) * mm, "end": v(19.75, 34.33) * mm});
            skLineSegment(sketch, "E16.right", {"start": v(14.75, 39.33) * mm, "end": v(14.75, 34.33) * mm});
            skSolve(sketch);
        }
        {
            var Q0;
            Q0=makeQuery(id+"F19.imprint","IMPRINT",FACE,{"disambiguationData":[TD([[makeQuery(id+"F19.imprint","IMPRINT",EDGE,{"derivedFrom":sQuery(id+"F19.wireOp",EDGE,"E16.bottom")}),1.0]])]});
            extrude(context, id + "F20", {"entities" : qUnion([Q0]), "operationType" : NewBodyOperationType.REMOVE, "oppositeDirection" : true, "depth" : 2.5 * mm, "offsetDistance" : 25 * mm});
        }
    });
